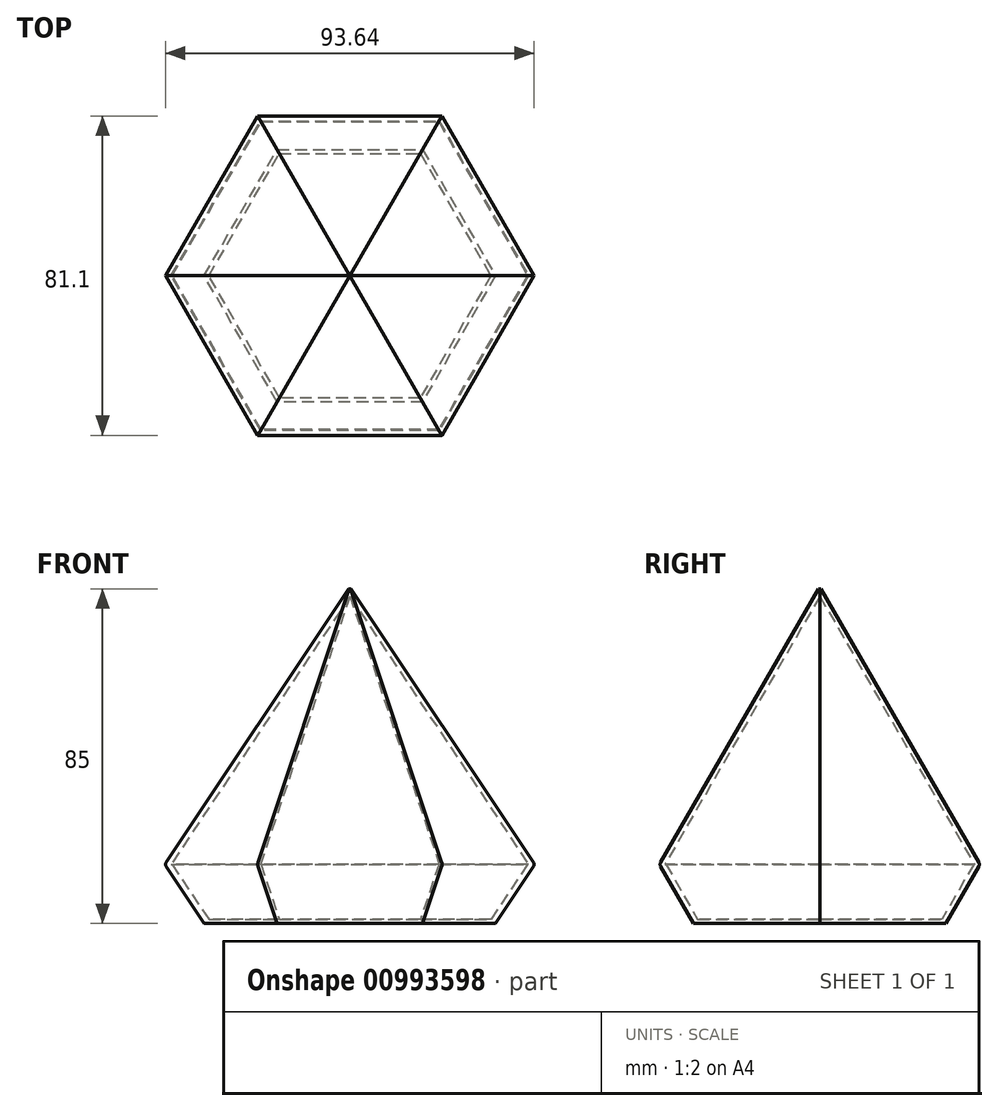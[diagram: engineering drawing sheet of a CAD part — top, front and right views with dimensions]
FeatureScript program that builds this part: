
annotation { "Feature Type Name" : "Feature", "Feature Type Description" : "" }
export const myFeature = defineFeature(function(context is Context, id is Id, definition is map)
    precondition{}
    {
        {
            var Q0;
            Q0=qCreatedBy(makeId("Top.planeOp"),FACE);
            var sketch = newSketch(context, id + "F0", { "sketchPlane" : qUnion([Q0])});
            skCircle(sketch, "E0.cCircle", {"center": v(0, 0) * mm, "radius": 30.44 * mm, "construction": true});
            skLineSegment(sketch, "E0.0", {"start": v(35.15, 0) * mm, "end": v(17.58, -30.44) * mm});
            skLineSegment(sketch, "E0.1", {"start": v(17.58, -30.44) * mm, "end": v(-17.58, -30.44) * mm});
            skLineSegment(sketch, "E0.2", {"start": v(-17.58, -30.44) * mm, "end": v(-35.15, 0) * mm});
            skLineSegment(sketch, "E0.3", {"start": v(-35.15, 0) * mm, "end": v(-17.58, 30.44) * mm});
            skLineSegment(sketch, "E0.4", {"start": v(-17.58, 30.44) * mm, "end": v(17.58, 30.44) * mm});
            skLineSegment(sketch, "E0.5", {"start": v(17.58, 30.44) * mm, "end": v(35.15, 0) * mm});
            skPoint(sketch, "E0.0.midPoint", {"position": v(26.36, -15.22) * mm});
            skLineSegment(sketch, "E1.0", {"start": v(-37, 0) * mm, "end": v(-18.5, 32.04) * mm});
            skLineSegment(sketch, "E1.1", {"start": v(18.5, 32.04) * mm, "end": v(37, 0) * mm});
            skLineSegment(sketch, "E1.2", {"start": v(37, 0) * mm, "end": v(18.5, -32.04) * mm});
            skLineSegment(sketch, "E1.3", {"start": v(-18.5, 32.04) * mm, "end": v(18.5, 32.04) * mm});
            skLineSegment(sketch, "E1.4", {"start": v(18.5, -32.04) * mm, "end": v(-18.5, -32.04) * mm});
            skLineSegment(sketch, "E1.5", {"start": v(-18.5, -32.04) * mm, "end": v(-37, 0) * mm});
            skSolve(sketch);
        }
        {
            var Q0;
            Q0=makeQuery(id+"F0.imprint","IMPRINT",FACE,{"disambiguationData":[TD([[makeQuery(id+"F0.imprint","IMPRINT",EDGE,{"derivedFrom":sQuery(id+"F0.wireOp",EDGE,"E0.0")}),1.0]])]});
            extrude(context, id + "F1", {"entities" : qUnion([Q0]), "depth" : 15 * mm, "offsetDistance" : 25 * mm, "hasDraft" : true, "draftAngle" : 30 * degree});
        }
        {
            var Q0;
            Q0=makeQuery(id+"F0.imprint","IMPRINT",FACE,{"disambiguationData":[TD([[makeQuery(id+"F0.imprint","IMPRINT",EDGE,{"derivedFrom":sQuery(id+"F0.wireOp",EDGE,"E0.0")}),-1.0]])]});
            extrude(context, id + "F2", {"entities" : qUnion([Q0]), "operationType" : NewBodyOperationType.REMOVE, "depth" : 15 * mm, "offsetDistance" : 25 * mm, "hasDraft" : true, "draftAngle" : 30 * degree});
        }
        {
            var Q0;
            Q0=makeQuery(id+"F0.imprint","IMPRINT",FACE,{"disambiguationData":[TD([[makeQuery(id+"F0.imprint","IMPRINT",EDGE,{"derivedFrom":sQuery(id+"F0.wireOp",EDGE,"E0.0")}),-1.0]])]});
            extrude(context, id + "F3", {"entities" : qUnion([Q0]), "operationType" : NewBodyOperationType.ADD, "depth" : 1 * mm, "offsetDistance" : 25 * mm, "hasDraft" : true, "draftAngle" : 35 * degree});
        }
        {
            var Q0;
            Q0=makeQuery(id+"F1.opExtrude","CAP_FACE",FACE,{"disambiguationData":[OSD([sQuery(id+"F0.wireOp",EDGE,"E0.0"),sQuery(id+"F0.wireOp",EDGE,"E0.1"),sQuery(id+"F0.wireOp",EDGE,"E0.2"),sQuery(id+"F0.wireOp",EDGE,"E0.3"),sQuery(id+"F0.wireOp",EDGE,"E0.4"),sQuery(id+"F0.wireOp",EDGE,"E0.5"),sQuery(id+"F0.wireOp",EDGE,"E1.0"),sQuery(id+"F0.wireOp",EDGE,"E1.1"),sQuery(id+"F0.wireOp",EDGE,"E1.2"),sQuery(id+"F0.wireOp",EDGE,"E1.3"),sQuery(id+"F0.wireOp",EDGE,"E1.4"),sQuery(id+"F0.wireOp",EDGE,"E1.5")])],"isStart":false});
            var sketch = newSketch(context, id + "F4", { "sketchPlane" : qUnion([Q0])});
            skCircle(sketch, "E2.cCircle", {"center": v(0, 0) * mm, "radius": 40.7 * mm, "construction": true});
            skLineSegment(sketch, "E2.0", {"start": v(47, 0) * mm, "end": v(23.5, -40.7) * mm});
            skLineSegment(sketch, "E2.1", {"start": v(23.5, -40.7) * mm, "end": v(-23.5, -40.7) * mm});
            skLineSegment(sketch, "E2.2", {"start": v(-23.5, -40.7) * mm, "end": v(-47, 0) * mm});
            skLineSegment(sketch, "E2.3", {"start": v(-47, 0) * mm, "end": v(-23.5, 40.7) * mm});
            skLineSegment(sketch, "E2.4", {"start": v(-23.5, 40.7) * mm, "end": v(23.5, 40.7) * mm});
            skLineSegment(sketch, "E2.5", {"start": v(23.5, 40.7) * mm, "end": v(47, 0) * mm});
            skPoint(sketch, "E2.0.midPoint", {"position": v(35.25, -20.35) * mm});
            skSolve(sketch);
        }
        {
            var Q0;
            Q0 = qSketchRegion(id + "F4", true);
            extrude(context, id + "F5", {"entities" : qUnion([Q0]), "depth" : 70 * mm, "offsetDistance" : 25 * mm, "hasDraft" : true, "draftAngle" : 30 * degree, "draftPullDirection" : true});
        }
        {
            var Q0;
            Q0=makeQuery(id+"F5.opExtrude","CAP_FACE",FACE,{"disambiguationData":[OSD([sQuery(id+"F4.wireOp",EDGE,"E2.0"),sQuery(id+"F4.wireOp",EDGE,"E2.1"),sQuery(id+"F4.wireOp",EDGE,"E2.2"),sQuery(id+"F4.wireOp",EDGE,"E2.3"),sQuery(id+"F4.wireOp",EDGE,"E2.4"),sQuery(id+"F4.wireOp",EDGE,"E2.5")])],"isStart":true});
            var sketch = newSketch(context, id + "F6", { "sketchPlane" : qUnion([Q0])});
            skCircle(sketch, "E3.cCircle", {"center": v(0, 0) * mm, "radius": 39.32 * mm, "construction": true});
            skLineSegment(sketch, "E3.0", {"start": v(22.7, 39.32) * mm, "end": v(45.4, 0) * mm});
            skLineSegment(sketch, "E3.1", {"start": v(45.4, 0) * mm, "end": v(22.7, -39.32) * mm});
            skLineSegment(sketch, "E3.2", {"start": v(22.7, -39.32) * mm, "end": v(-22.7, -39.32) * mm});
            skLineSegment(sketch, "E3.3", {"start": v(-22.7, -39.32) * mm, "end": v(-45.4, 0) * mm});
            skLineSegment(sketch, "E3.4", {"start": v(-45.4, 0) * mm, "end": v(-22.7, 39.32) * mm});
            skLineSegment(sketch, "E3.5", {"start": v(-22.7, 39.32) * mm, "end": v(22.7, 39.32) * mm});
            skPoint(sketch, "E3.0.midPoint", {"position": v(34.05, 19.66) * mm});
            skSolve(sketch);
        }
        {
            var Q0;
            Q0 = qSketchRegion(id + "F6", true);
            extrude(context, id + "F7", {"entities" : qUnion([Q0]), "operationType" : NewBodyOperationType.REMOVE, "oppositeDirection" : true, "depth" : 70 * mm, "offsetDistance" : 25 * mm, "hasDraft" : true, "draftAngle" : 30 * degree, "draftPullDirection" : true});
        }
        {
            var Q0;
            Q0=makeQuery(id+"F1.opExtrude","SWEPT_BODY",BODY,{"disambiguationData":[OSD([sQuery(id+"F0.wireOp",EDGE,"E0.0"),sQuery(id+"F0.wireOp",EDGE,"E0.1"),sQuery(id+"F0.wireOp",EDGE,"E0.2"),sQuery(id+"F0.wireOp",EDGE,"E0.3"),sQuery(id+"F0.wireOp",EDGE,"E0.4"),sQuery(id+"F0.wireOp",EDGE,"E0.5"),sQuery(id+"F0.wireOp",EDGE,"E1.0"),sQuery(id+"F0.wireOp",EDGE,"E1.1"),sQuery(id+"F0.wireOp",EDGE,"E1.2"),sQuery(id+"F0.wireOp",EDGE,"E1.3"),sQuery(id+"F0.wireOp",EDGE,"E1.4"),sQuery(id+"F0.wireOp",EDGE,"E1.5")])]});
            var Q1;
            Q1=makeQuery(id+"F5.opExtrude","SWEPT_BODY",BODY,{"disambiguationData":[OSD([sQuery(id+"F4.wireOp",EDGE,"E2.0"),sQuery(id+"F4.wireOp",EDGE,"E2.1"),sQuery(id+"F4.wireOp",EDGE,"E2.2"),sQuery(id+"F4.wireOp",EDGE,"E2.3"),sQuery(id+"F4.wireOp",EDGE,"E2.4"),sQuery(id+"F4.wireOp",EDGE,"E2.5")])]});
            booleanBodies(context, id + "F8", {"operationType" : BooleanOperationType.UNION, "tools" : qUnion([Q0, Q1])});
        }
        {
            var Q0;
            Q0=makeQuery(id+"F8.opBoolean","MERGE",EDGE,{"derivedFrom":[makeQuery(id+"F1.opExtrude","CAP_EDGE",EDGE,{"disambiguationData":[OSD([sQuery(id+"F0.wireOp",EDGE,"E1.4")])],"isStart":false}),makeQuery(id+"F5.opExtrude","CAP_EDGE",EDGE,{"disambiguationData":[OSD([sQuery(id+"F4.wireOp",EDGE,"E2.1")])],"isStart":true})]});
            var Q1;
            Q1=makeQuery(id+"F8.opBoolean","MERGE",EDGE,{"derivedFrom":[makeQuery(id+"F1.opExtrude","CAP_EDGE",EDGE,{"disambiguationData":[OSD([sQuery(id+"F0.wireOp",EDGE,"E1.2")])],"isStart":false}),makeQuery(id+"F5.opExtrude","CAP_EDGE",EDGE,{"disambiguationData":[OSD([sQuery(id+"F4.wireOp",EDGE,"E2.0")])],"isStart":true})]});
            var Q2;
            Q2=makeQuery(id+"F8.opBoolean","MERGE",EDGE,{"derivedFrom":[makeQuery(id+"F1.opExtrude","CAP_EDGE",EDGE,{"disambiguationData":[OSD([sQuery(id+"F0.wireOp",EDGE,"E1.1")])],"isStart":false}),makeQuery(id+"F5.opExtrude","CAP_EDGE",EDGE,{"disambiguationData":[OSD([sQuery(id+"F4.wireOp",EDGE,"E2.5")])],"isStart":true})]});
            var Q3;
            Q3=makeQuery(id+"F8.opBoolean","MERGE",EDGE,{"derivedFrom":[makeQuery(id+"F1.opExtrude","CAP_EDGE",EDGE,{"disambiguationData":[OSD([sQuery(id+"F0.wireOp",EDGE,"E1.3")])],"isStart":false}),makeQuery(id+"F5.opExtrude","CAP_EDGE",EDGE,{"disambiguationData":[OSD([sQuery(id+"F4.wireOp",EDGE,"E2.4")])],"isStart":true})]});
            var Q4;
            Q4=makeQuery(id+"F8.opBoolean","MERGE",EDGE,{"derivedFrom":[makeQuery(id+"F1.opExtrude","CAP_EDGE",EDGE,{"disambiguationData":[OSD([sQuery(id+"F0.wireOp",EDGE,"E1.0")])],"isStart":false}),makeQuery(id+"F5.opExtrude","CAP_EDGE",EDGE,{"disambiguationData":[OSD([sQuery(id+"F4.wireOp",EDGE,"E2.3")])],"isStart":true})]});
            var Q5;
            Q5=makeQuery(id+"F8.opBoolean","MERGE",EDGE,{"derivedFrom":[makeQuery(id+"F1.opExtrude","CAP_EDGE",EDGE,{"disambiguationData":[OSD([sQuery(id+"F0.wireOp",EDGE,"E1.5")])],"isStart":false}),makeQuery(id+"F5.opExtrude","CAP_EDGE",EDGE,{"disambiguationData":[OSD([sQuery(id+"F4.wireOp",EDGE,"E2.2")])],"isStart":true})]});
            fillet(context, id + "F9", {"entities" : qUnion([Q0, Q1, Q2, Q3, Q4, Q5]), "tangentPropagation" : true, "radius" : 1 * mm, "defaultsChanged" : true, "vertexSettings" : [], "allowEdgeOverflow" : false});
        }
    });
